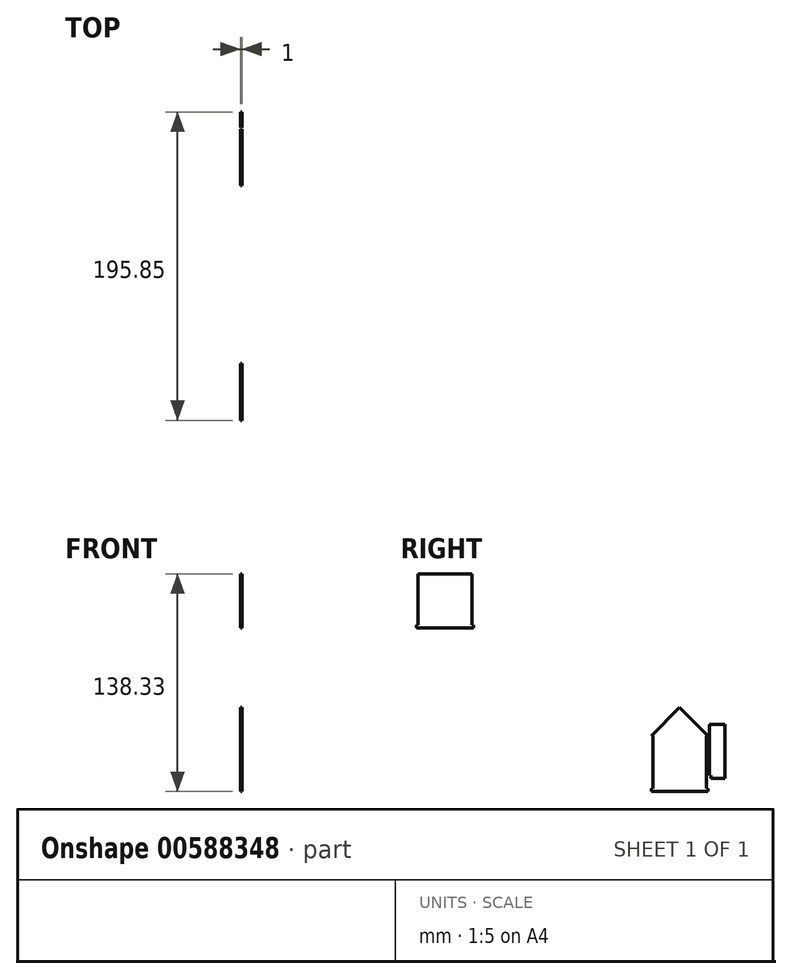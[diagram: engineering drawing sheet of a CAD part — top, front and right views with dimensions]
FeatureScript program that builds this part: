
annotation { "Feature Type Name" : "Feature", "Feature Type Description" : "" }
export const myFeature = defineFeature(function(context is Context, id is Id, definition is map)
    precondition{}
    {
        {
            var Q0;
            Q0=qCreatedBy(makeId("Right.planeOp"),FACE);
            var sketch = newSketch(context, id + "F0", { "sketchPlane" : qUnion([Q0])});
            skLineSegment(sketch, "E0", {"start": v(35.4, 69.26) * mm, "end": v(17.4, 51.26) * mm});
            skLineSegment(sketch, "E1", {"start": v(35.4, 69.26) * mm, "end": v(53.4, 51.26) * mm});
            skLineSegment(sketch, "E2", {"start": v(31.4, 51.26) * mm, "end": v(39.4, 51.26) * mm});
            skLineSegment(sketch, "E3", {"start": v(35.4, 51.26) * mm, "end": v(39.4, 51.26) * mm});
            skLineSegment(sketch, "E4", {"start": v(39.4, 43.26) * mm, "end": v(31.4, 43.26) * mm});
            skLineSegment(sketch, "E5", {"start": v(31.4, 43.26) * mm, "end": v(31.4, 51.26) * mm});
            skPoint(sketch, "E6.end.orphan", {"position": v(35.4, 24.26) * mm});
            skLineSegment(sketch, "E7", {"start": v(17.4, 51.26) * mm, "end": v(18.4, 51.26) * mm});
            skLineSegment(sketch, "E8", {"start": v(18.4, 51.26) * mm, "end": v(18.4, 26.26) * mm});
            skLineSegment(sketch, "E9", {"start": v(53.4, 51.26) * mm, "end": v(52.4, 51.26) * mm});
            skLineSegment(sketch, "E10", {"start": v(52.4, 51.26) * mm, "end": v(52.4, 26.26) * mm});
            skPoint(sketch, "E11.orphan", {"position": v(53.4, 24.26) * mm});
            skPoint(sketch, "E12.orphan", {"position": v(17.4, 24.26) * mm});
            skLineSegment(sketch, "E13", {"start": v(55.17, 24.26) * mm, "end": v(55.17, 26.26) * mm});
            skLineSegment(sketch, "E14", {"start": v(55.17, 26.26) * mm, "end": v(54.17, 26.26) * mm});
            skLineSegment(sketch, "E15", {"start": v(54.17, 26.26) * mm, "end": v(54.17, 56.69) * mm});
            skLineSegment(sketch, "E16", {"start": v(55.17, 24.26) * mm, "end": v(62.17, 24.26) * mm});
            skLineSegment(sketch, "E17.MirrorCS", {"start": v(76.47, 26.26) * mm, "end": v(77.17, 26.26) * mm});
            skLineSegment(sketch, "E18.MirrorCS", {"start": v(76.47, 24.26) * mm, "end": v(76.47, 26.26) * mm});
            skLineSegment(sketch, "E19.MirrorCS", {"start": v(76.47, 24.26) * mm, "end": v(69.17, 24.26) * mm});
            skLineSegment(sketch, "E20", {"start": v(53.4, 17.86) * mm, "end": v(53.4, 15.86) * mm});
            skLineSegment(sketch, "E21", {"start": v(53.4, 15.86) * mm, "end": v(12.53, 15.86) * mm});
            skLineSegment(sketch, "E22", {"start": v(17.4, 17.86) * mm, "end": v(17.4, 15.86) * mm});
            skLineSegment(sketch, "E23", {"start": v(17.4, 15.86) * mm, "end": v(17.4, 17.86) * mm});
            skLineSegment(sketch, "E24", {"start": v(17.4, 17.86) * mm, "end": v(18.4, 17.86) * mm});
            skLineSegment(sketch, "E25", {"start": v(18.4, 17.86) * mm, "end": v(18.4, 26.26) * mm});
            skLineSegment(sketch, "E26", {"start": v(52.4, 17.86) * mm, "end": v(53.4, 17.86) * mm});
            skLineSegment(sketch, "E27", {"start": v(52.4, 24.26) * mm, "end": v(52.4, 17.86) * mm});
            skLineSegment(sketch, "E28", {"start": v(52.4, 24.26) * mm, "end": v(52.4, 26.26) * mm});
            skLineSegment(sketch, "E29", {"start": v(77.17, 57.66) * mm, "end": v(77.17, 59.66) * mm});
            skLineSegment(sketch, "E30", {"start": v(69.17, 59.66) * mm, "end": v(77.17, 59.66) * mm});
            skLineSegment(sketch, "E31", {"start": v(54.17, 56.69) * mm, "end": v(54.17, 58.69) * mm});
            skLineSegment(sketch, "E32", {"start": v(54.17, 58.69) * mm, "end": v(62.17, 58.69) * mm});
            skLineSegment(sketch, "E33", {"start": v(69.17, 24.26) * mm, "end": v(67.17, 24.26) * mm});
            skLineSegment(sketch, "E34", {"start": v(69.17, 59.66) * mm, "end": v(67.17, 59.66) * mm});
            skLineSegment(sketch, "E35", {"start": v(67.17, 59.66) * mm, "end": v(67.17, 24.26) * mm});
            skLineSegment(sketch, "E36", {"start": v(67.17, 24.26) * mm, "end": v(62.17, 24.26) * mm});
            skLineSegment(sketch, "E37", {"start": v(62.17, 24.26) * mm, "end": v(64.67, 24.26) * mm});
            skLineSegment(sketch, "E38", {"start": v(62.17, 58.69) * mm, "end": v(64.17, 58.69) * mm});
            skLineSegment(sketch, "E39", {"start": v(64.17, 58.69) * mm, "end": v(64.17, 20.24) * mm});
            skLineSegment(sketch, "E40.0", {"start": v(-160.45, 114.76) * mm, "end": v(-135.8, 149.85) * mm});
            skPoint(sketch, "E41.0", {"position": v(-134.35, 151.37) * mm});
            skLineSegment(sketch, "E42.0", {"start": v(-132.9, 152.9) * mm, "end": v(-113.68, 173.16) * mm});
            skLineSegment(sketch, "E43.0", {"start": v(-113.68, 173.16) * mm, "end": v(-94.45, 152.9) * mm});
            skPoint(sketch, "E44.0", {"position": v(-93, 151.37) * mm});
            skLineSegment(sketch, "E45.0", {"start": v(-91.56, 149.85) * mm, "end": v(-66.9, 114.76) * mm});
            skLineSegment(sketch, "E46.0", {"start": v(-237.63, 91.39) * mm, "end": v(15.38, 91.39) * mm});
            skPoint(sketch, "E47.0", {"position": v(-99.62, 91.39) * mm});
            skLineSegment(sketch, "E48", {"start": v(-113.68, 173.16) * mm, "end": v(-113.68, 75) * mm});
            skLineSegment(sketch, "E49", {"start": v(-94.45, 152.9) * mm, "end": v(-93, 151.37) * mm});
            skLineSegment(sketch, "E50", {"start": v(-91.56, 149.85) * mm, "end": v(-93, 151.37) * mm});
            skLineSegment(sketch, "E51", {"start": v(-132.9, 152.9) * mm, "end": v(-134.35, 151.37) * mm});
            skLineSegment(sketch, "E52", {"start": v(-135.8, 149.85) * mm, "end": v(-134.35, 151.37) * mm});
            skLineSegment(sketch, "E53", {"start": v(-113.68, 173.16) * mm, "end": v(-113.68, 119.76) * mm});
            skLineSegment(sketch, "E54", {"start": v(-113.68, 119.76) * mm, "end": v(-131.68, 119.76) * mm});
            skLineSegment(sketch, "E55", {"start": v(-131.68, 119.76) * mm, "end": v(-131.68, 121.76) * mm});
            skLineSegment(sketch, "E56", {"start": v(-113.68, 119.76) * mm, "end": v(-95.68, 119.76) * mm});
            skLineSegment(sketch, "E57", {"start": v(-95.68, 119.76) * mm, "end": v(-95.68, 121.76) * mm});
            skLineSegment(sketch, "E58", {"start": v(-95.68, 154.19) * mm, "end": v(-131.68, 154.19) * mm});
            skLineSegment(sketch, "E59", {"start": v(-95.68, 154.19) * mm, "end": v(-96.68, 154.19) * mm});
            skLineSegment(sketch, "E60", {"start": v(-96.68, 154.19) * mm, "end": v(-96.68, 118.43) * mm});
            skLineSegment(sketch, "E61", {"start": v(-131.68, 154.19) * mm, "end": v(-130.68, 154.19) * mm});
            skLineSegment(sketch, "E62", {"start": v(-130.68, 154.19) * mm, "end": v(-130.68, 118.62) * mm});
            skLineSegment(sketch, "E63", {"start": v(-131.68, 121.76) * mm, "end": v(-130.68, 121.76) * mm});
            skLineSegment(sketch, "E64", {"start": v(-95.68, 121.76) * mm, "end": v(-96.68, 121.76) * mm});
            skLineSegment(sketch, "E65.trimOffspring", {"start": v(-95.68, 154.19) * mm, "end": v(-95.68, 165.13) * mm});
            skLineSegment(sketch, "E66.trimOffspring", {"start": v(-131.68, 154.19) * mm, "end": v(-131.68, 163.17) * mm});
            skSolve(sketch);
        }
        {
            var Q0;
            Q0=makeQuery(id+"F0.imprint","IMPRINT",FACE,{"disambiguationData":[TD([[makeQuery(id+"F0.imprint","IMPRINT",EDGE,{"derivedFrom":sQuery(id+"F0.wireOp",EDGE,"E17.MirrorCS")}),1.0]])]});
            var Q1;
            Q1=makeQuery(id+"F0.imprint","IMPRINT",FACE,{"disambiguationData":[TD([[makeQuery(id+"F0.imprint","IMPRINT",EDGE,{"derivedFrom":sQuery(id+"F0.wireOp",EDGE,"E13")}),-1.0]])]});
            var Q2;
            Q2=makeQuery(id+"F0.imprint","IMPRINT",FACE,{"disambiguationData":[TD([[makeQuery(id+"F0.imprint","IMPRINT",EDGE,{"derivedFrom":sQuery(id+"F0.wireOp",EDGE,"E0")}),1.0]])]});
            extrude(context, id + "F1", {"entities" : qUnion([Q0, Q1, Q2]), "depth" : 1 * mm, "offsetDistance" : 25 * mm});
        }
        {
            var Q0;
            {var subQ0=sQuery(id+"F0.wireOp",EDGE,"E60");var subQ3=makeQuery(id+"F0.imprint","INTERSECT",VERTEX,{"derivedFrom":[subQ0,sQuery(id+"F0.wireOp",EDGE,"E64")]});Q0=makeQuery(id+"F0.imprint","IMPRINT",FACE,{"disambiguationData":[TD([[makeQuery(id+"F0.imprint","IMPRINT",EDGE,{"disambiguationData":[TD([[subQ3,-1.0]])],"derivedFrom":subQ0}),-1.0]])]});}
            var Q1;
            {var subQ3=sQuery(id+"F0.wireOp",EDGE,"E59");Q1=makeQuery(id+"F0.imprint","IMPRINT",FACE,{"disambiguationData":[TD([[makeQuery(id+"F0.imprint","IMPRINT",EDGE,{"derivedFrom":subQ3}),-1.0]])]});}
            var Q2;
            {var subQ3=sQuery(id+"F0.wireOp",EDGE,"E61");Q2=makeQuery(id+"F0.imprint","IMPRINT",FACE,{"disambiguationData":[TD([[makeQuery(id+"F0.imprint","IMPRINT",EDGE,{"derivedFrom":subQ3}),1.0]])]});}
            var Q3;
            {var subQ0=sQuery(id+"F0.wireOp",EDGE,"E62");var subQ3=makeQuery(id+"F0.imprint","INTERSECT",VERTEX,{"derivedFrom":[subQ0,sQuery(id+"F0.wireOp",EDGE,"E63")]});Q3=makeQuery(id+"F0.imprint","IMPRINT",FACE,{"disambiguationData":[TD([[makeQuery(id+"F0.imprint","IMPRINT",EDGE,{"disambiguationData":[TD([[subQ3,-1.0]])],"derivedFrom":subQ0}),1.0]])]});}
            extrude(context, id + "F2", {"entities" : qUnion([Q0, Q1, Q2, Q3]), "depth" : 1 * mm, "offsetDistance" : 25 * mm});
        }
        {
            var Q0;
            {var subQ0=sQuery(id+"F0.wireOp",EDGE,"E55");Q0=makeQuery(id+"F0.imprint","IMPRINT",FACE,{"disambiguationData":[TD([[makeQuery(id+"F0.imprint","IMPRINT",EDGE,{"derivedFrom":subQ0}),-1.0]])]});}
            var Q1;
            {var subQ0=sQuery(id+"F0.wireOp",EDGE,"E57");Q1=makeQuery(id+"F0.imprint","IMPRINT",FACE,{"disambiguationData":[TD([[makeQuery(id+"F0.imprint","IMPRINT",EDGE,{"derivedFrom":subQ0}),1.0]])]});}
            extrude(context, id + "F3", {"entities" : qUnion([Q0, Q1]), "operationType" : NewBodyOperationType.ADD, "depth" : 1 * mm, "offsetDistance" : 25 * mm});
        }
    });
